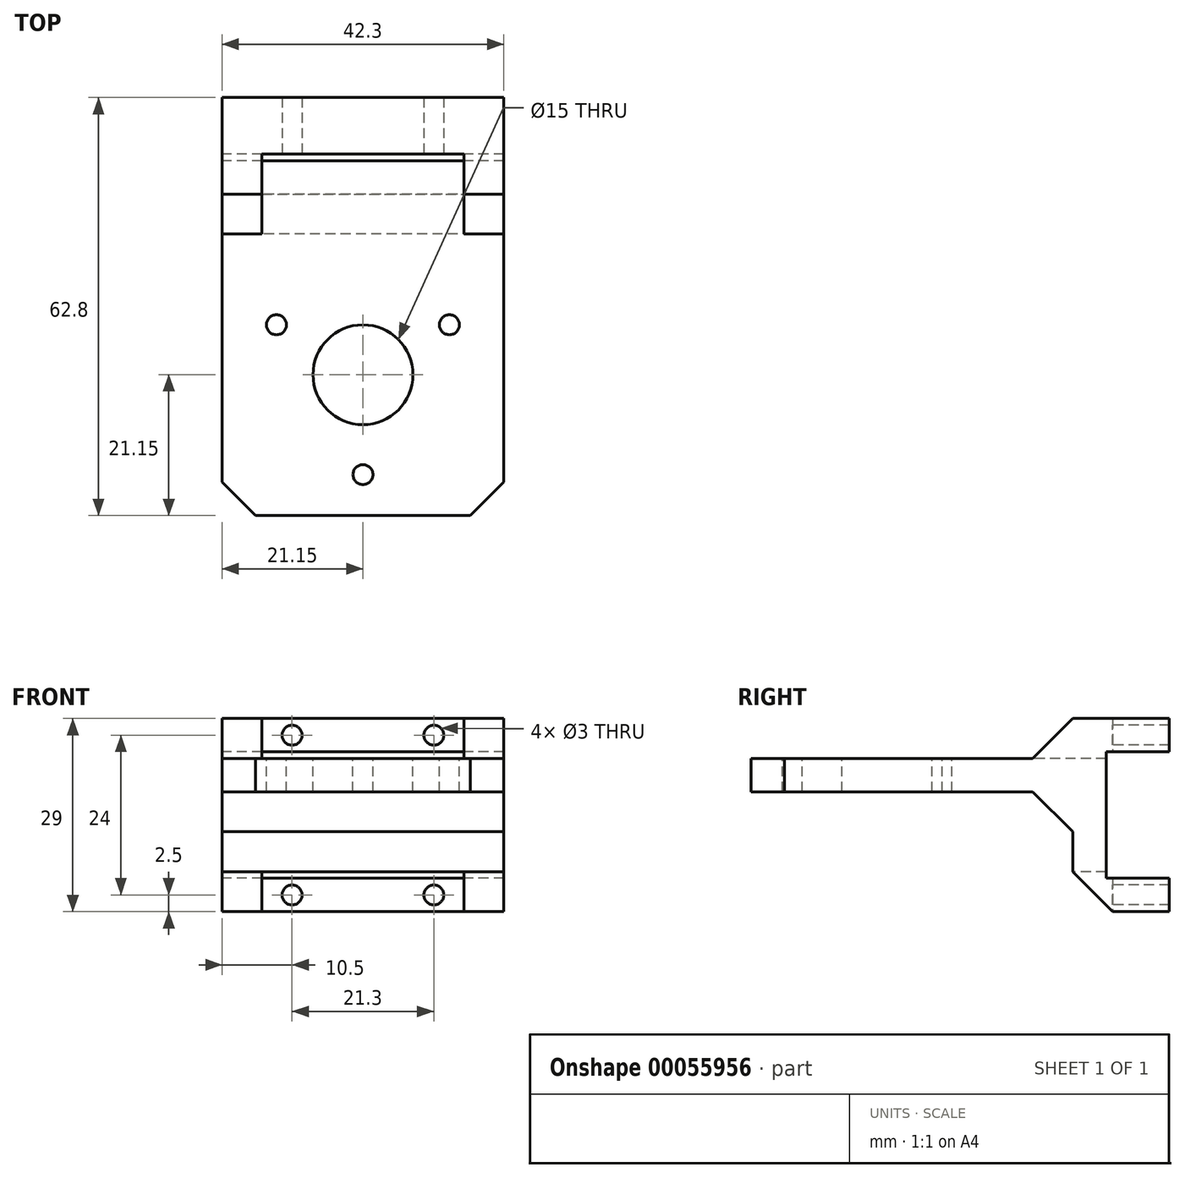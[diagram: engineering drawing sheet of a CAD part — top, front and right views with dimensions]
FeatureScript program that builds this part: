
annotation { "Feature Type Name" : "Feature", "Feature Type Description" : "" }
export const myFeature = defineFeature(function(context is Context, id is Id, definition is map)
    precondition{}
    {
        {
            var Q0;
            Q0=qCreatedBy(makeId("Right.planeOp"),FACE);
            var sketch = newSketch(context, id + "F0", { "sketchPlane" : qUnion([Q0])});
            skLineSegment(sketch, "E0.rect.bottom", {"start": v(0, 9.5) * mm, "end": v(-9.5, 9.5) * mm});
            skLineSegment(sketch, "E0.rect.top", {"start": v(0, -9.5) * mm, "end": v(-9.5, -9.5) * mm});
            skLineSegment(sketch, "E0.rect.right", {"start": v(-9.5, 9.5) * mm, "end": v(-9.5, -9.5) * mm});
            skPoint(sketch, "E0.rect.middle", {"position": v(0, 0) * mm});
            skLineSegment(sketch, "E1.rect.bottom", {"start": v(0, 14.5) * mm, "end": v(-14.5, 14.5) * mm});
            skLineSegment(sketch, "E1.rect.top", {"start": v(0, -14.5) * mm, "end": v(-14.5, -14.5) * mm});
            skLineSegment(sketch, "E2", {"start": v(-14.5, 14.5) * mm, "end": v(-14.5, 8.5) * mm, "construction": true});
            skLineSegment(sketch, "E3", {"start": v(-14.5, 8.5) * mm, "end": v(-14.5, 3.5) * mm, "construction": true});
            skLineSegment(sketch, "E4", {"start": v(-14.5, 3.5) * mm, "end": v(-14.5, -2.5) * mm, "construction": true});
            skLineSegment(sketch, "E5", {"start": v(-14.5, -2.5) * mm, "end": v(-14.5, -14.5) * mm});
            skLineSegment(sketch, "E6.bottom", {"start": v(-14.5, 8.5) * mm, "end": v(-20.5, 8.5) * mm, "construction": true});
            skLineSegment(sketch, "E6.top", {"start": v(-14.5, 3.5) * mm, "end": v(-20.5, 3.5) * mm, "construction": true});
            skLineSegment(sketch, "E6.right", {"start": v(-20.5, 8.5) * mm, "end": v(-20.5, 3.5) * mm, "construction": true});
            skLineSegment(sketch, "E7.bottom", {"start": v(-20.5, 8.5) * mm, "end": v(-62.8, 8.5) * mm});
            skLineSegment(sketch, "E7.top", {"start": v(-20.5, 3.5) * mm, "end": v(-62.8, 3.5) * mm});
            skLineSegment(sketch, "E7.right", {"start": v(-62.8, 8.5) * mm, "end": v(-62.8, 3.5) * mm});
            skLineSegment(sketch, "E8.bottom", {"start": v(-14.5, 14.5) * mm, "end": v(-20.5, 14.5) * mm});
            skLineSegment(sketch, "E8.right", {"start": v(-20.5, 14.5) * mm, "end": v(-20.5, 8.5) * mm});
            skLineSegment(sketch, "E9.bottom", {"start": v(-14.5, -2.5) * mm, "end": v(-20.5, -2.5) * mm});
            skLineSegment(sketch, "E9.right", {"start": v(-20.5, -2.5) * mm, "end": v(-20.5, 3.5) * mm});
            skLineSegment(sketch, "E10", {"start": v(0, 9.5) * mm, "end": v(0, 14.5) * mm});
            skLineSegment(sketch, "E11", {"start": v(0, -9.5) * mm, "end": v(0, -14.5) * mm});
            skSolve(sketch);
        }
        {
            var Q0;
            Q0=makeQuery(id+"F0.imprint","IMPRINT",FACE,{"disambiguationData":[TD([[makeQuery(id+"F0.imprint","IMPRINT",EDGE,{"derivedFrom":sQuery(id+"F0.wireOp",EDGE,"5346ee42-6b44-4ab4-b06a-5ea702be0697.bottom")}),1.0]])]});
            var Q1;
            Q1=makeQuery(id+"F0.imprint","IMPRINT",FACE,{"disambiguationData":[TD([[makeQuery(id+"F0.imprint","IMPRINT",EDGE,{"derivedFrom":sQuery(id+"F0.wireOp",EDGE,"9599e187-f427-41b1-8912-62db417e26b9.bottom")}),1.0]])]});
            var Q2;
            Q2=makeQuery(id+"F0.imprint","IMPRINT",FACE,{"disambiguationData":[TD([[makeQuery(id+"F0.imprint","IMPRINT",EDGE,{"derivedFrom":sQuery(id+"F0.wireOp",EDGE,"E0.rect.bottom")}),-1.0]])]});
            extrude(context, id + "F1", {"entities" : qUnion([Q0, Q1, Q2]), "depth" : 42.3 * mm});
        }
        {
            var Q0;
            Q0=makeQuery(id+"F1.opExtrude","SWEPT_FACE",FACE,{"disambiguationData":[OSD([sQuery(id+"F0.wireOp",EDGE,"E8.right")])]});
            var sketch = newSketch(context, id + "F2", { "sketchPlane" : qUnion([Q0])});
            skLineSegment(sketch, "E12.bottom", {"start": v(0, 14.5) * mm, "end": v(6, 14.5) * mm, "construction": true});
            skLineSegment(sketch, "E12.top", {"start": v(0, 8.5) * mm, "end": v(6, 8.5) * mm, "construction": true});
            skLineSegment(sketch, "E12.left", {"start": v(0, 14.5) * mm, "end": v(0, 8.5) * mm, "construction": true});
            skLineSegment(sketch, "E12.right", {"start": v(6, 14.5) * mm, "end": v(6, 8.5) * mm, "construction": true});
            skLineSegment(sketch, "E13.bottom", {"start": v(42.3, 14.5) * mm, "end": v(36.3, 14.5) * mm, "construction": true});
            skLineSegment(sketch, "E13.top", {"start": v(42.3, 8.5) * mm, "end": v(36.3, 8.5) * mm, "construction": true});
            skLineSegment(sketch, "E13.left", {"start": v(42.3, 14.5) * mm, "end": v(42.3, 8.5) * mm, "construction": true});
            skLineSegment(sketch, "E13.right", {"start": v(36.3, 14.5) * mm, "end": v(36.3, 8.5) * mm, "construction": true});
            skLineSegment(sketch, "E14.bottom", {"start": v(6, 14.5) * mm, "end": v(36.3, 14.5) * mm});
            skLineSegment(sketch, "E14.top", {"start": v(6, 8.5) * mm, "end": v(36.3, 8.5) * mm});
            skLineSegment(sketch, "E14.left", {"start": v(6, 14.5) * mm, "end": v(6, 8.5) * mm});
            skLineSegment(sketch, "E14.right", {"start": v(36.3, 14.5) * mm, "end": v(36.3, 8.5) * mm});
            skSolve(sketch);
        }
        {
            var Q0;
            Q0=makeQuery(id+"F1.opExtrude","SWEPT_FACE",FACE,{"disambiguationData":[OSD([sQuery(id+"F0.wireOp",EDGE,"E5")])]});
            var sketch = newSketch(context, id + "F3", { "sketchPlane" : qUnion([Q0])});
            skLineSegment(sketch, "E15.bottom", {"start": v(0, -14.5) * mm, "end": v(6, -14.5) * mm, "construction": true});
            skLineSegment(sketch, "E15.top", {"start": v(0, -8.5) * mm, "end": v(6, -8.5) * mm, "construction": true});
            skLineSegment(sketch, "E15.left", {"start": v(0, -14.5) * mm, "end": v(0, -8.5) * mm, "construction": true});
            skLineSegment(sketch, "E15.right", {"start": v(6, -14.5) * mm, "end": v(6, -8.5) * mm, "construction": true});
            skLineSegment(sketch, "E16.bottom", {"start": v(42.3, -14.5) * mm, "end": v(36.3, -14.5) * mm, "construction": true});
            skLineSegment(sketch, "E16.top", {"start": v(42.3, -8.54) * mm, "end": v(36.3, -8.54) * mm, "construction": true});
            skLineSegment(sketch, "E16.left", {"start": v(42.3, -14.5) * mm, "end": v(42.3, -8.54) * mm, "construction": true});
            skLineSegment(sketch, "E16.right", {"start": v(36.3, -14.5) * mm, "end": v(36.3, -8.54) * mm, "construction": true});
            skLineSegment(sketch, "E17.bottom", {"start": v(6, -8.5) * mm, "end": v(36.3, -8.5) * mm});
            skLineSegment(sketch, "E17.top", {"start": v(6, -14.5) * mm, "end": v(36.3, -14.5) * mm});
            skLineSegment(sketch, "E17.left", {"start": v(6, -8.5) * mm, "end": v(6, -14.5) * mm});
            skLineSegment(sketch, "E17.right", {"start": v(36.3, -8.5) * mm, "end": v(36.3, -14.5) * mm});
            skSolve(sketch);
        }
        {
            var Q0;
            Q0=makeQuery(id+"F3.imprint","IMPRINT",FACE,{"disambiguationData":[TD([[makeQuery(id+"F3.imprint","IMPRINT",EDGE,{"derivedFrom":sQuery(id+"F3.wireOp",EDGE,"E17.bottom")}),-1.0]])]});
            extrude(context, id + "F4", {"entities" : qUnion([Q0]), "operationType" : NewBodyOperationType.REMOVE, "oppositeDirection" : true, "depth" : 6 * mm});
        }
        {
            var Q0;
            Q0=makeQuery(id+"F2.imprint","IMPRINT",FACE,{"disambiguationData":[TD([[makeQuery(id+"F2.imprint","IMPRINT",EDGE,{"derivedFrom":sQuery(id+"F2.wireOp",EDGE,"E14.bottom")}),1.0]])]});
            extrude(context, id + "F5", {"entities" : qUnion([Q0]), "operationType" : NewBodyOperationType.REMOVE, "oppositeDirection" : true, "depth" : 12 * mm});
        }
        {
            var Q0;
            {var subQ0=sQuery(id+"F0.wireOp",EDGE,"E5");var subQ1=sQuery(id+"F0.wireOp",EDGE,"E1.rect.top");Q0=makeQuery(id+"F4.boolean.opBoolean","SPLIT",EDGE,{"disambiguationData":[TD([makeQuery(id+"F4.opExtrude","SWEPT_FACE",FACE,{"disambiguationData":[OSD([sQuery(id+"F3.wireOp",EDGE,"E17.left")])]})])],"derivedFrom":makeQuery(id+"F1.opExtrude","SWEPT_EDGE",EDGE,{"disambiguationData":[OSD([subQ1,subQ0])]})});}
            var Q1;
            {var subQ0=sQuery(id+"F0.wireOp",EDGE,"E5");var subQ1=sQuery(id+"F0.wireOp",EDGE,"E1.rect.top");Q1=makeQuery(id+"F4.boolean.opBoolean","SPLIT",EDGE,{"disambiguationData":[TD([makeQuery(id+"F4.opExtrude","SWEPT_FACE",FACE,{"disambiguationData":[OSD([sQuery(id+"F3.wireOp",EDGE,"E17.right")])]})])],"derivedFrom":makeQuery(id+"F1.opExtrude","SWEPT_EDGE",EDGE,{"disambiguationData":[OSD([subQ1,subQ0])]})});}
            var Q2;
            {var subQ0=sQuery(id+"F0.wireOp",EDGE,"E5");var subQ1=sQuery(id+"F0.wireOp",EDGE,"E1.rect.top");Q2=makeQuery(id+"F4.boolean.opBoolean","SPLIT",EDGE,{"disambiguationData":[TD([makeQuery(id+"F4.opExtrude","SWEPT_FACE",FACE,{"disambiguationData":[OSD([sQuery(id+"F3.wireOp",EDGE,"E17.left")])]})])],"derivedFrom":makeQuery(id+"F1.opExtrude","SWEPT_EDGE",EDGE,{"disambiguationData":[OSD([subQ1,subQ0])]})});}
            var Q3;
            {var subQ0=sQuery(id+"F0.wireOp",EDGE,"E5");var subQ1=sQuery(id+"F0.wireOp",EDGE,"E1.rect.top");Q3=makeQuery(id+"F4.boolean.opBoolean","SPLIT",EDGE,{"disambiguationData":[TD([makeQuery(id+"F4.opExtrude","SWEPT_FACE",FACE,{"disambiguationData":[OSD([sQuery(id+"F3.wireOp",EDGE,"E17.right")])]})])],"derivedFrom":makeQuery(id+"F1.opExtrude","SWEPT_EDGE",EDGE,{"disambiguationData":[OSD([subQ1,subQ0])]})});}
            var Q4;
            {var subQ0=sQuery(id+"F0.wireOp",EDGE,"E8.right");var subQ1=sQuery(id+"F0.wireOp",EDGE,"E8.bottom");Q4=makeQuery(id+"F5.boolean.opBoolean","SPLIT",EDGE,{"disambiguationData":[TD([makeQuery(id+"F5.opExtrude","SWEPT_FACE",FACE,{"disambiguationData":[OSD([sQuery(id+"F2.wireOp",EDGE,"E14.left")])]})])],"derivedFrom":makeQuery(id+"F1.opExtrude","SWEPT_EDGE",EDGE,{"disambiguationData":[OSD([subQ1,subQ0])]})});}
            var Q5;
            {var subQ0=sQuery(id+"F0.wireOp",EDGE,"E8.right");var subQ1=sQuery(id+"F0.wireOp",EDGE,"E8.bottom");Q5=makeQuery(id+"F5.boolean.opBoolean","SPLIT",EDGE,{"disambiguationData":[TD([makeQuery(id+"F5.opExtrude","SWEPT_FACE",FACE,{"disambiguationData":[OSD([sQuery(id+"F2.wireOp",EDGE,"E14.right")])]})])],"derivedFrom":makeQuery(id+"F1.opExtrude","SWEPT_EDGE",EDGE,{"disambiguationData":[OSD([subQ1,subQ0])]})});}
            var Q6;
            Q6=makeQuery(id+"F1.opExtrude","SWEPT_EDGE",EDGE,{"disambiguationData":[OSD([sQuery(id+"F0.wireOp",EDGE,"E9.bottom"),sQuery(id+"F0.wireOp",EDGE,"E9.right")])]});
            var Q7;
            {var subQ0=sQuery(id+"F0.wireOp",EDGE,"E5");var subQ1=sQuery(id+"F0.wireOp",EDGE,"E1.rect.top");Q7=makeQuery(id+"F4.boolean.opBoolean","SPLIT",EDGE,{"disambiguationData":[TD([makeQuery(id+"F4.opExtrude","SWEPT_FACE",FACE,{"disambiguationData":[OSD([sQuery(id+"F3.wireOp",EDGE,"E17.left")])]})])],"derivedFrom":makeQuery(id+"F1.opExtrude","SWEPT_EDGE",EDGE,{"disambiguationData":[OSD([subQ1,subQ0])]})});}
            var Q8;
            {var subQ0=sQuery(id+"F0.wireOp",EDGE,"E5");var subQ1=sQuery(id+"F0.wireOp",EDGE,"E1.rect.top");Q8=makeQuery(id+"F4.boolean.opBoolean","SPLIT",EDGE,{"disambiguationData":[TD([makeQuery(id+"F4.opExtrude","SWEPT_FACE",FACE,{"disambiguationData":[OSD([sQuery(id+"F3.wireOp",EDGE,"E17.right")])]})])],"derivedFrom":makeQuery(id+"F1.opExtrude","SWEPT_EDGE",EDGE,{"disambiguationData":[OSD([subQ1,subQ0])]})});}
            var Q9;
            {var subQ0=sQuery(id+"F0.wireOp",EDGE,"E5");var subQ1=sQuery(id+"F0.wireOp",EDGE,"E1.rect.top");Q9=makeQuery(id+"F4.boolean.opBoolean","SPLIT",EDGE,{"disambiguationData":[TD([makeQuery(id+"F4.opExtrude","SWEPT_FACE",FACE,{"disambiguationData":[OSD([sQuery(id+"F3.wireOp",EDGE,"E17.left")])]})])],"derivedFrom":makeQuery(id+"F1.opExtrude","SWEPT_EDGE",EDGE,{"disambiguationData":[OSD([subQ1,subQ0])]})});}
            var Q10;
            {var subQ0=sQuery(id+"F0.wireOp",EDGE,"E5");var subQ1=sQuery(id+"F0.wireOp",EDGE,"E1.rect.top");Q10=makeQuery(id+"F4.boolean.opBoolean","SPLIT",EDGE,{"disambiguationData":[TD([makeQuery(id+"F4.opExtrude","SWEPT_FACE",FACE,{"disambiguationData":[OSD([sQuery(id+"F3.wireOp",EDGE,"E17.right")])]})])],"derivedFrom":makeQuery(id+"F1.opExtrude","SWEPT_EDGE",EDGE,{"disambiguationData":[OSD([subQ1,subQ0])]})});}
            chamfer(context, id + "F6", {"entities" : qUnion([Q0, Q1, Q2, Q3, Q4, Q5, Q6, Q7, Q8, Q9, Q10]), "width" : 6 * mm, "tangentPropagation" : true});
        }
        {
            var Q0;
            Q0=makeQuery(id+"F5.boolean.opBoolean","COPY",FACE,{"derivedFrom":makeQuery(id+"F5.opExtrude","CAP_FACE",FACE,{"disambiguationData":[OSD([sQuery(id+"F2.wireOp",EDGE,"E14.bottom"),sQuery(id+"F2.wireOp",EDGE,"E14.top"),sQuery(id+"F2.wireOp",EDGE,"E14.left"),sQuery(id+"F2.wireOp",EDGE,"E14.right")])],"isStart":false})});
            var sketch = newSketch(context, id + "F7", { "sketchPlane" : qUnion([Q0])});
            skLineSegment(sketch, "E18.bottom", {"start": v(6, 14.5) * mm, "end": v(8, 14.5) * mm, "construction": true});
            skLineSegment(sketch, "E18.top", {"start": v(6, 9.5) * mm, "end": v(8, 9.5) * mm, "construction": true});
            skLineSegment(sketch, "E18.left", {"start": v(6, 14.5) * mm, "end": v(6, 9.5) * mm, "construction": true});
            skLineSegment(sketch, "E18.right", {"start": v(8, 14.5) * mm, "end": v(8, 9.5) * mm, "construction": true});
            skLineSegment(sketch, "E19.bottom", {"start": v(36.3, 14.5) * mm, "end": v(34.3, 14.5) * mm, "construction": true});
            skLineSegment(sketch, "E19.top", {"start": v(36.3, 9.5) * mm, "end": v(34.3, 9.5) * mm, "construction": true});
            skLineSegment(sketch, "E19.left", {"start": v(36.3, 14.5) * mm, "end": v(36.3, 9.5) * mm, "construction": true});
            skLineSegment(sketch, "E19.right", {"start": v(34.3, 14.5) * mm, "end": v(34.3, 9.5) * mm, "construction": true});
            skLineSegment(sketch, "E20.bottom", {"start": v(8, 14.5) * mm, "end": v(13, 14.5) * mm, "construction": true});
            skLineSegment(sketch, "E20.top", {"start": v(8, 9.5) * mm, "end": v(13, 9.5) * mm, "construction": true});
            skLineSegment(sketch, "E20.right", {"start": v(13, 14.5) * mm, "end": v(13, 9.5) * mm, "construction": true});
            skLineSegment(sketch, "E21.bottom", {"start": v(34.3, 14.5) * mm, "end": v(29.3, 14.5) * mm, "construction": true});
            skLineSegment(sketch, "E21.top", {"start": v(34.3, 9.5) * mm, "end": v(29.3, 9.5) * mm, "construction": true});
            skLineSegment(sketch, "E21.right", {"start": v(29.3, 14.5) * mm, "end": v(29.3, 9.5) * mm, "construction": true});
            skLineSegment(sketch, "E22", {"start": v(8, 14.5) * mm, "end": v(13, 9.5) * mm, "construction": true});
            skLineSegment(sketch, "E23", {"start": v(29.3, 14.5) * mm, "end": v(34.3, 9.5) * mm, "construction": true});
            skCircle(sketch, "E24", {"center": v(10.5, 12) * mm, "radius": 1.5 * mm});
            skCircle(sketch, "E25", {"center": v(31.8, 12) * mm, "radius": 1.5 * mm});
            skSolve(sketch);
        }
        {
            var Q0;
            Q0=makeQuery(id+"F7.imprint","IMPRINT",FACE,{"disambiguationData":[TD([[makeQuery(id+"F7.imprint","IMPRINT",EDGE,{"derivedFrom":sQuery(id+"F7.wireOp",EDGE,"E24")}),1.0]])]});
            var Q1;
            Q1=makeQuery(id+"F7.imprint","IMPRINT",FACE,{"disambiguationData":[TD([[makeQuery(id+"F7.imprint","IMPRINT",EDGE,{"derivedFrom":sQuery(id+"F7.wireOp",EDGE,"E25")}),1.0]])]});
            extrude(context, id + "F8", {"entities" : qUnion([Q0, Q1]), "operationType" : NewBodyOperationType.REMOVE, "endBound" : BoundingType.THROUGH_ALL, "oppositeDirection" : true, "depth" : 25 * mm});
        }
        {
            var Q0;
            Q0=makeQuery(id+"F4.boolean.opBoolean","COPY",FACE,{"derivedFrom":makeQuery(id+"F4.opExtrude","CAP_FACE",FACE,{"disambiguationData":[OSD([sQuery(id+"F3.wireOp",EDGE,"E17.bottom"),sQuery(id+"F3.wireOp",EDGE,"E17.top"),sQuery(id+"F3.wireOp",EDGE,"E17.left"),sQuery(id+"F3.wireOp",EDGE,"E17.right")])],"isStart":false})});
            var sketch = newSketch(context, id + "F9", { "sketchPlane" : qUnion([Q0])});
            skLineSegment(sketch, "E26", {"start": v(6, -9.5) * mm, "end": v(8, -9.5) * mm, "construction": true});
            skLineSegment(sketch, "E27", {"start": v(8, -9.5) * mm, "end": v(13, -9.5) * mm, "construction": true});
            skLineSegment(sketch, "E28", {"start": v(36.3, -9.5) * mm, "end": v(34.3, -9.5) * mm, "construction": true});
            skLineSegment(sketch, "E29", {"start": v(34.3, -9.5) * mm, "end": v(29.3, -9.5) * mm, "construction": true});
            skLineSegment(sketch, "E30", {"start": v(8, -9.5) * mm, "end": v(13, -14.5) * mm, "construction": true});
            skLineSegment(sketch, "E31", {"start": v(29.3, -9.5) * mm, "end": v(34.3, -14.5) * mm, "construction": true});
            skCircle(sketch, "E32", {"center": v(10.5, -12) * mm, "radius": 1.5 * mm});
            skCircle(sketch, "E33", {"center": v(31.8, -12) * mm, "radius": 1.5 * mm});
            skSolve(sketch);
        }
        {
            var Q0;
            Q0=makeQuery(id+"F9.imprint","IMPRINT",FACE,{"disambiguationData":[TD([[makeQuery(id+"F9.imprint","IMPRINT",EDGE,{"derivedFrom":sQuery(id+"F9.wireOp",EDGE,"E32")}),1.0]])]});
            var Q1;
            Q1=makeQuery(id+"F9.imprint","IMPRINT",FACE,{"disambiguationData":[TD([[makeQuery(id+"F9.imprint","IMPRINT",EDGE,{"derivedFrom":sQuery(id+"F9.wireOp",EDGE,"E33")}),1.0]])]});
            extrude(context, id + "F10", {"entities" : qUnion([Q0, Q1]), "operationType" : NewBodyOperationType.REMOVE, "endBound" : BoundingType.THROUGH_ALL, "oppositeDirection" : true, "depth" : 25 * mm});
        }
        {
            var Q0;
            Q0=makeQuery(id+"F5.boolean.opBoolean","MERGE",FACE,{"derivedFrom":[makeQuery(id+"F1.opExtrude","SWEPT_FACE",FACE,{"disambiguationData":[OSD([sQuery(id+"F0.wireOp",EDGE,"E7.bottom")])]}),makeQuery(id+"F5.opExtrude","SWEPT_FACE",FACE,{"disambiguationData":[OSD([sQuery(id+"F2.wireOp",EDGE,"E14.top")])]})]});
            var sketch = newSketch(context, id + "F11", { "sketchPlane" : qUnion([Q0])});
            skLineSegment(sketch, "E34", {"start": v(42.3, -62.8) * mm, "end": v(0, -20.5) * mm, "construction": true});
            skCircle(sketch, "E35", {"center": v(21.15, -41.65) * mm, "radius": 7.5 * mm});
            skCircle(sketch, "E36.cCircle", {"center": v(21.15, -41.65) * mm, "radius": 7.5 * mm, "construction": true});
            skLineSegment(sketch, "E36.0", {"start": v(8.16, -34.15) * mm, "end": v(34.14, -34.15) * mm, "construction": true});
            skLineSegment(sketch, "E36.1", {"start": v(34.14, -34.15) * mm, "end": v(21.15, -56.65) * mm, "construction": true});
            skLineSegment(sketch, "E36.2", {"start": v(21.15, -56.65) * mm, "end": v(8.16, -34.15) * mm, "construction": true});
            skPoint(sketch, "E36.0.midPoint", {"position": v(21.15, -34.15) * mm});
            skCircle(sketch, "E37", {"center": v(8.16, -34.15) * mm, "radius": 1.5 * mm});
            skCircle(sketch, "E38", {"center": v(34.14, -34.15) * mm, "radius": 1.5 * mm});
            skCircle(sketch, "E39", {"center": v(21.15, -56.65) * mm, "radius": 1.5 * mm});
            skSolve(sketch);
        }
        {
            var Q0;
            Q0=makeQuery(id+"F11.imprint","IMPRINT",FACE,{"disambiguationData":[TD([[makeQuery(id+"F11.imprint","IMPRINT",EDGE,{"derivedFrom":sQuery(id+"F11.wireOp",EDGE,"E37")}),1.0]])]});
            var Q1;
            Q1=makeQuery(id+"F11.imprint","IMPRINT",FACE,{"disambiguationData":[TD([[makeQuery(id+"F11.imprint","IMPRINT",EDGE,{"derivedFrom":sQuery(id+"F11.wireOp",EDGE,"E35")}),1.0]])]});
            var Q2;
            Q2=makeQuery(id+"F11.imprint","IMPRINT",FACE,{"disambiguationData":[TD([[makeQuery(id+"F11.imprint","IMPRINT",EDGE,{"derivedFrom":sQuery(id+"F11.wireOp",EDGE,"E38")}),1.0]])]});
            var Q3;
            Q3=makeQuery(id+"F11.imprint","IMPRINT",FACE,{"disambiguationData":[TD([[makeQuery(id+"F11.imprint","IMPRINT",EDGE,{"derivedFrom":sQuery(id+"F11.wireOp",EDGE,"E39")}),1.0]])]});
            extrude(context, id + "F12", {"entities" : qUnion([Q0, Q1, Q2, Q3]), "operationType" : NewBodyOperationType.REMOVE, "endBound" : BoundingType.UP_TO_NEXT, "oppositeDirection" : true, "depth" : 25 * mm});
        }
        {
            var Q0;
            Q0=makeQuery(id+"F1.opExtrude","CAP_EDGE",EDGE,{"disambiguationData":[OSD([sQuery(id+"F0.wireOp",EDGE,"E7.right")])],"isStart":false});
            var Q1;
            Q1=makeQuery(id+"F1.opExtrude","CAP_EDGE",EDGE,{"disambiguationData":[OSD([sQuery(id+"F0.wireOp",EDGE,"E7.right")])],"isStart":true});
            chamfer(context, id + "F13", {"entities" : qUnion([Q0, Q1]), "width" : 5 * mm, "tangentPropagation" : true});
        }
    });
